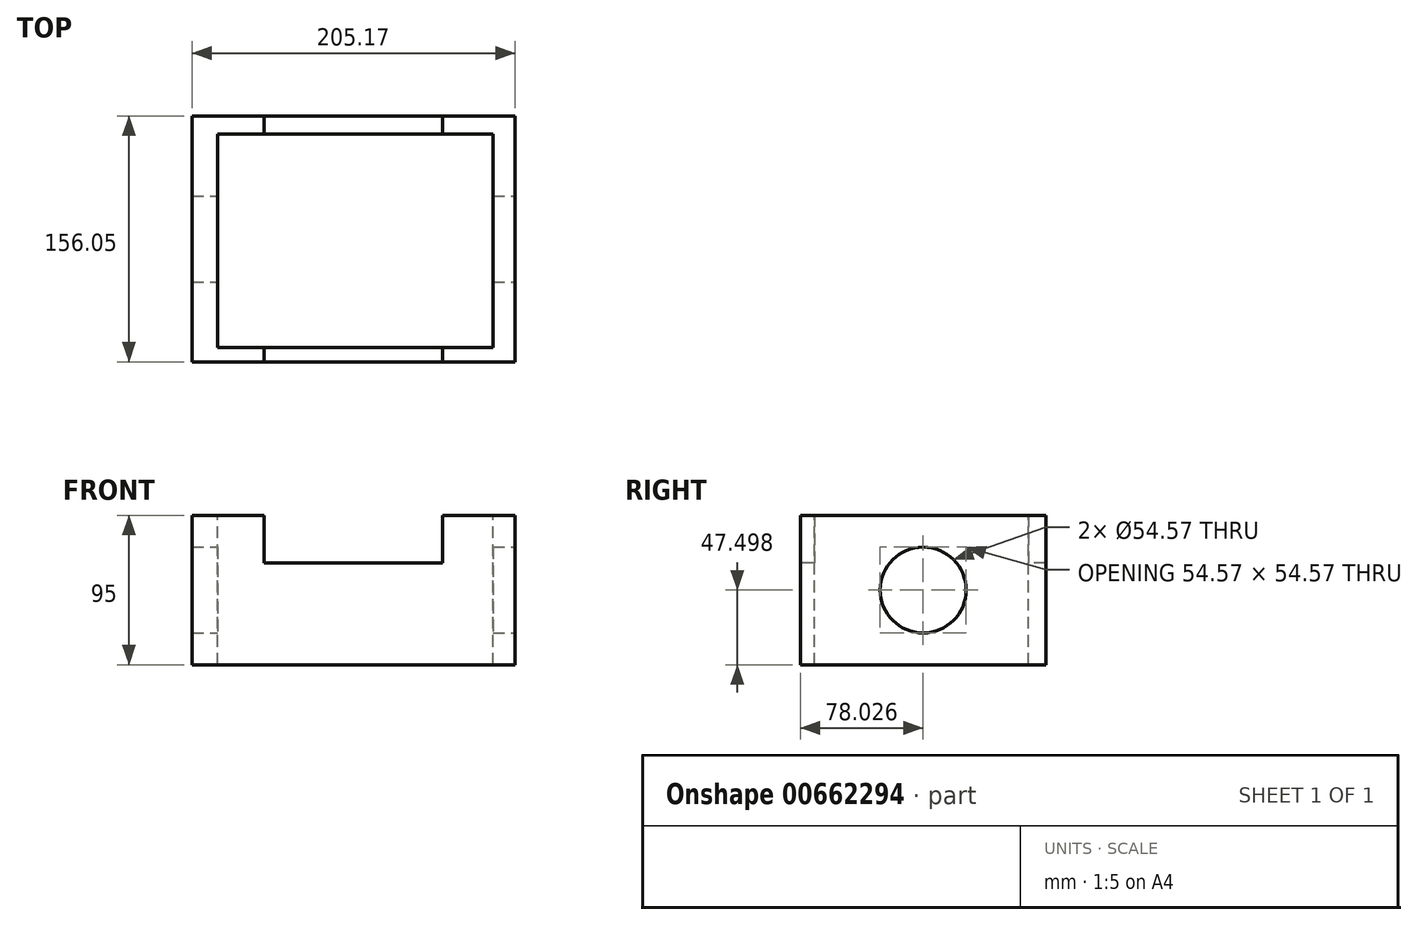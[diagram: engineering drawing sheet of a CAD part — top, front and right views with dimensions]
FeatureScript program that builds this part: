
annotation { "Feature Type Name" : "Feature", "Feature Type Description" : "" }
export const myFeature = defineFeature(function(context is Context, id is Id, definition is map)
    precondition{}
    {
        {
            var Q0;
            Q0=qCreatedBy(makeId("Top.planeOp"),FACE);
            var sketch = newSketch(context, id + "F0", { "sketchPlane" : qUnion([Q0])});
            skLineSegment(sketch, "E0.bottom", {"start": v(-92.19, 68.85) * mm, "end": v(112.98, 68.85) * mm});
            skLineSegment(sketch, "E0.top", {"start": v(-92.19, -87.2) * mm, "end": v(112.98, -87.2) * mm});
            skLineSegment(sketch, "E0.left", {"start": v(-92.19, 68.85) * mm, "end": v(-92.19, -87.2) * mm});
            skLineSegment(sketch, "E0.right", {"start": v(112.98, 68.85) * mm, "end": v(112.98, -87.2) * mm});
            skSolve(sketch);
        }
        {
            var Q0;
            Q0 = qSketchRegion(id + "F0", true);
            extrude(context, id + "F1", {"entities" : qUnion([Q0]), "depth" : 95 * mm, "offsetDistance" : 25.4 * mm});
        }
        {
            var Q0;
            Q0=makeQuery(id+"F1.opExtrude","CAP_FACE",FACE,{"disambiguationData":[OSD([sQuery(id+"F0.wireOp",EDGE,"E0.bottom"),sQuery(id+"F0.wireOp",EDGE,"E0.top"),sQuery(id+"F0.wireOp",EDGE,"E0.left"),sQuery(id+"F0.wireOp",EDGE,"E0.right")])],"isStart":false});
            var sketch = newSketch(context, id + "F2", { "sketchPlane" : qUnion([Q0])});
            skLineSegment(sketch, "E1.bottom", {"start": v(99.02, 57.57) * mm, "end": v(-76.04, 57.57) * mm});
            skLineSegment(sketch, "E1.top", {"start": v(99.02, -78.2) * mm, "end": v(-76.04, -78.2) * mm});
            skLineSegment(sketch, "E1.left", {"start": v(99.02, 57.57) * mm, "end": v(99.02, -78.2) * mm});
            skLineSegment(sketch, "E1.right", {"start": v(-76.04, 57.57) * mm, "end": v(-76.04, -78.2) * mm});
            skPoint(sketch, "E1.middle", {"position": v(11.49, -10.32) * mm});
            skSolve(sketch);
        }
        {
            var Q0;
            Q0 = qSketchRegion(id + "F2", true);
            extrude(context, id + "F3", {"entities" : qUnion([Q0]), "operationType" : NewBodyOperationType.REMOVE, "oppositeDirection" : true, "depth" : 115.57 * mm, "offsetDistance" : 25.4 * mm});
        }
        {
            var Q0;
            Q0=makeQuery(id+"F1.opExtrude","SWEPT_FACE",FACE,{"disambiguationData":[OSD([sQuery(id+"F0.wireOp",EDGE,"E0.right")])]});
            var sketch = newSketch(context, id + "F4", { "sketchPlane" : qUnion([Q0])});
            skPoint(sketch, "E2.end.orphan", {"position": v(0, 43.13) * mm});
            skPoint(sketch, "E2.start.orphan", {"position": v(-9.17, 47.5) * mm});
            skCircle(sketch, "E3", {"center": v(-9.17, 47.5) * mm, "radius": 27.28 * mm});
            skPoint(sketch, "E4.orphan", {"position": v(-87.2, 47.5) * mm});
            skPoint(sketch, "E5.orphan", {"position": v(68.85, 47.5) * mm});
            skSolve(sketch);
        }
        {
            var Q0;
            Q0=makeQuery(id+"F4.imprint","IMPRINT",FACE,{"disambiguationData":[TD([[makeQuery(id+"F4.imprint","IMPRINT",EDGE,{"derivedFrom":sQuery(id+"F4.wireOp",EDGE,"E3")}),1.0]])]});
            extrude(context, id + "F5", {"entities" : qUnion([Q0]), "operationType" : NewBodyOperationType.REMOVE, "endBound" : BoundingType.THROUGH_ALL, "oppositeDirection" : true, "depth" : 25.4 * mm, "offsetDistance" : 25.4 * mm});
        }
        {
            var Q0;
            Q0=makeQuery(id+"F1.opExtrude","SWEPT_FACE",FACE,{"disambiguationData":[OSD([sQuery(id+"F0.wireOp",EDGE,"E0.top")])]});
            var sketch = newSketch(context, id + "F6", { "sketchPlane" : qUnion([Q0])});
            skLineSegment(sketch, "E6.bottom", {"start": v(67.14, 64.57) * mm, "end": v(-46.34, 64.57) * mm});
            skLineSegment(sketch, "E6.top", {"start": v(67.14, 125.42) * mm, "end": v(-46.34, 125.42) * mm});
            skLineSegment(sketch, "E6.left", {"start": v(67.14, 64.57) * mm, "end": v(67.14, 125.42) * mm});
            skLineSegment(sketch, "E6.right", {"start": v(-46.34, 64.57) * mm, "end": v(-46.34, 125.42) * mm});
            skPoint(sketch, "E6.middle", {"position": v(10.4, 95) * mm});
            skSolve(sketch);
        }
        {
            var Q0;
            Q0 = qSketchRegion(id + "F6", true);
            extrude(context, id + "F7", {"entities" : qUnion([Q0]), "operationType" : NewBodyOperationType.REMOVE, "endBound" : BoundingType.THROUGH_ALL, "oppositeDirection" : true, "depth" : 25.4 * mm, "offsetDistance" : 25.4 * mm});
        }
    });
